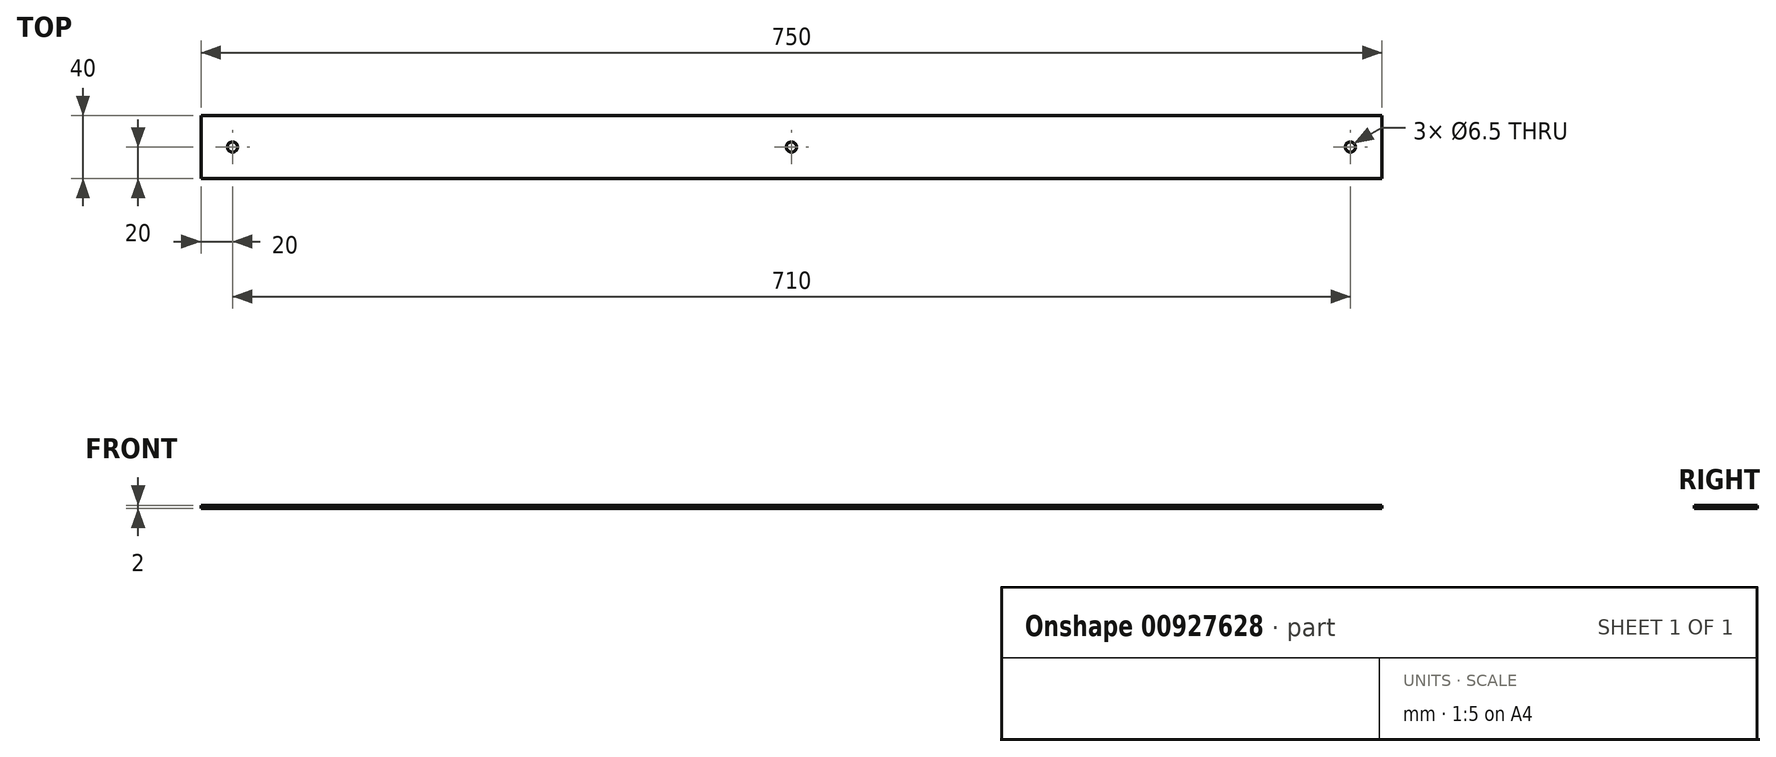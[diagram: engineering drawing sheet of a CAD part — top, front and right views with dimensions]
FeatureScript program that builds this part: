
annotation { "Feature Type Name" : "Feature", "Feature Type Description" : "" }
export const myFeature = defineFeature(function(context is Context, id is Id, definition is map)
    precondition{}
    {
        {
            var Q0;
            Q0=qCreatedBy(makeId("Right.planeOp"),FACE);
            var sketch = newSketch(context, id + "F0", { "sketchPlane" : qUnion([Q0])});
            skLineSegment(sketch, "E0.bottom", {"start": v(20, 1) * mm, "end": v(-20, 1) * mm});
            skLineSegment(sketch, "E0.top", {"start": v(20, -1) * mm, "end": v(-20, -1) * mm});
            skLineSegment(sketch, "E0.left", {"start": v(20, 1) * mm, "end": v(20, -1) * mm});
            skLineSegment(sketch, "E0.right", {"start": v(-20, 1) * mm, "end": v(-20, -1) * mm});
            skPoint(sketch, "E0.middle", {"position": v(0, 0) * mm});
            skSolve(sketch);
        }
        {
            var Q0;
            Q0 = qSketchRegion(id + "F0", true);
            extrude(context, id + "F1", {"entities" : qUnion([Q0]), "depth" : (400 + 350) * mm, "offsetDistance" : 25 * mm});
        }
        {
            var Q0;
            Q0=makeQuery(id+"F1.opExtrude","SWEPT_FACE",FACE,{"disambiguationData":[OSD([sQuery(id+"F0.wireOp",EDGE,"E0.bottom")])]});
            var sketch = newSketch(context, id + "F2", { "sketchPlane" : qUnion([Q0])});
            skLineSegment(sketch, "E1", {"start": v(-25.05, 0) * mm, "end": v(758.09, 0) * mm, "construction": true});
            skPoint(sketch, "E1.endSnap0", {"position": v(750, 0) * mm});
            skCircle(sketch, "E2", {"center": v(730, 0) * mm, "radius": 3.25 * mm});
            skLineSegment(sketch, "E3", {"start": v(375, 112.29) * mm, "end": v(375, -118.62) * mm, "construction": true});
            skPoint(sketch, "E3.startSnap0", {"position": v(375, 20) * mm});
            skCircle(sketch, "E4.MirrorC", {"center": v(20, 0) * mm, "radius": 3.25 * mm});
            skPoint(sketch, "E5", {"position": v(375, 0) * mm});
            skCircle(sketch, "E6", {"center": v(375, 0) * mm, "radius": 3.25 * mm});
            skSolve(sketch);
        }
        {
            var Q0;
            Q0 = qSketchRegion(id + "F2", true);
            extrude(context, id + "F3", {"entities" : qUnion([Q0]), "operationType" : NewBodyOperationType.REMOVE, "oppositeDirection" : true, "depth" : 25 * mm, "offsetDistance" : 25 * mm});
        }
    });
